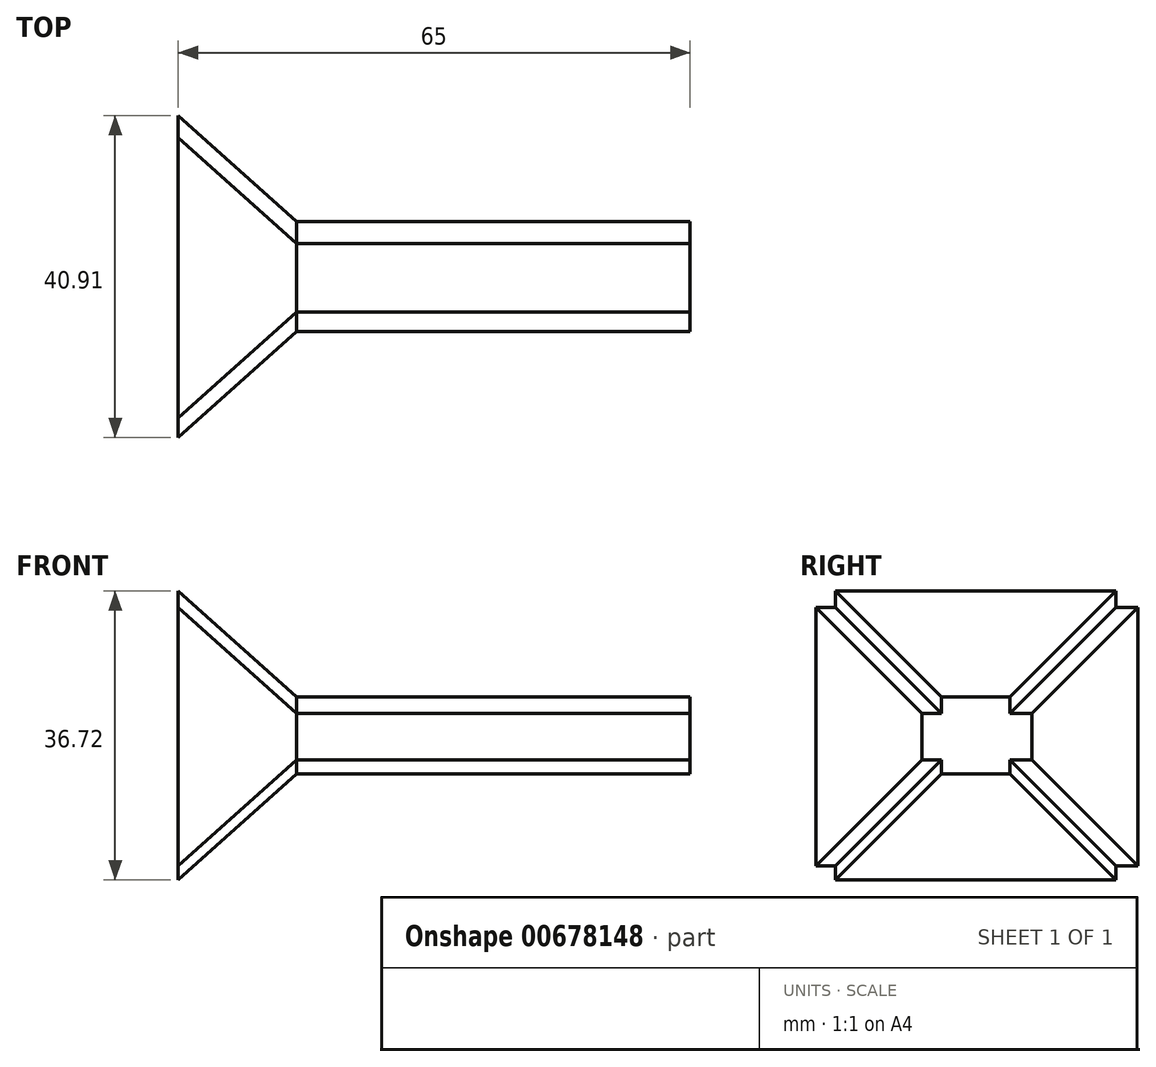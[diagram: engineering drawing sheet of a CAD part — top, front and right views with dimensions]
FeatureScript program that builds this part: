
annotation { "Feature Type Name" : "Feature", "Feature Type Description" : "" }
export const myFeature = defineFeature(function(context is Context, id is Id, definition is map)
    precondition{}
    {
        {
            var Q0;
            Q0=qCreatedBy(makeId("Right.planeOp"),FACE);
            var sketch = newSketch(context, id + "F0", { "sketchPlane" : qUnion([Q0])});
            skLineSegment(sketch, "E0.bottom", {"start": v(-4.45, 4.98) * mm, "end": v(4.28, 4.98) * mm});
            skLineSegment(sketch, "E0.top", {"start": v(-4.45, -4.82) * mm, "end": v(4.28, -4.82) * mm});
            skLineSegment(sketch, "E0.left", {"start": v(-4.45, 4.98) * mm, "end": v(-4.45, -4.82) * mm});
            skLineSegment(sketch, "E0.right", {"start": v(4.28, 4.98) * mm, "end": v(4.28, -4.82) * mm});
            skLineSegment(sketch, "E1.bottom", {"start": v(-6.9, 2.87) * mm, "end": v(7.08, 2.87) * mm});
            skLineSegment(sketch, "E1.top", {"start": v(-6.9, -3.03) * mm, "end": v(7.08, -3.03) * mm});
            skLineSegment(sketch, "E1.left", {"start": v(-6.9, 2.87) * mm, "end": v(-6.9, -3.03) * mm});
            skLineSegment(sketch, "E1.right", {"start": v(7.08, 2.87) * mm, "end": v(7.08, -3.03) * mm});
            skSolve(sketch);
        }
        {
            var Q0;
            {var subQ0=sQuery(id+"F0.wireOp",EDGE,"E0.bottom");Q0=makeQuery(id+"F0.imprint","IMPRINT",FACE,{"disambiguationData":[TD([[makeQuery(id+"F0.imprint","IMPRINT",EDGE,{"derivedFrom":subQ0}),-1.0]])]});}
            var Q1;
            {var subQ0=sQuery(id+"F0.wireOp",EDGE,"E0.top");Q1=makeQuery(id+"F0.imprint","IMPRINT",FACE,{"disambiguationData":[TD([[makeQuery(id+"F0.imprint","IMPRINT",EDGE,{"derivedFrom":subQ0}),1.0]])]});}
            var Q2;
            {var subQ5=sQuery(id+"F0.wireOp",EDGE,"E1.left");Q2=makeQuery(id+"F0.imprint","IMPRINT",FACE,{"disambiguationData":[TD([[makeQuery(id+"F0.imprint","IMPRINT",EDGE,{"derivedFrom":subQ5}),1.0]])]});}
            var Q3;
            {var subQ5=sQuery(id+"F0.wireOp",EDGE,"E1.right");Q3=makeQuery(id+"F0.imprint","IMPRINT",FACE,{"disambiguationData":[TD([[makeQuery(id+"F0.imprint","IMPRINT",EDGE,{"derivedFrom":subQ5}),-1.0]])]});}
            var Q4;
            {var subQ0=sQuery(id+"F0.wireOp",EDGE,"E1.bottom");var subQ1=sQuery(id+"F0.wireOp",EDGE,"E0.left");var subQ2=makeQuery(id+"F0.imprint","INTERSECT",VERTEX,{"derivedFrom":[subQ1,subQ0]});Q4=makeQuery(id+"F0.imprint","IMPRINT",FACE,{"disambiguationData":[TD([[makeQuery(id+"F0.imprint","IMPRINT",EDGE,{"disambiguationData":[TD([[subQ2,-1.0]])],"derivedFrom":subQ1}),1.0]])]});}
            extrude(context, id + "F1", {"entities" : qUnion([Q0, Q1, Q2, Q3, Q4]), "depth" : 50 * mm, "offsetDistance" : 25 * mm});
        }
        {
            var Q0;
            Q0=makeQuery(id+"F1.opExtrude","CAP_FACE",FACE,{"disambiguationData":[OSD([sQuery(id+"F0.wireOp",EDGE,"E0.bottom"),sQuery(id+"F0.wireOp",EDGE,"E0.top"),sQuery(id+"F0.wireOp",EDGE,"E0.left"),sQuery(id+"F0.wireOp",EDGE,"E0.right"),sQuery(id+"F0.wireOp",EDGE,"E1.bottom"),sQuery(id+"F0.wireOp",EDGE,"E1.top"),sQuery(id+"F0.wireOp",EDGE,"E1.left"),sQuery(id+"F0.wireOp",EDGE,"E1.right")])],"isStart":true});
            extrude(context, id + "F2", {"entities" : qUnion([Q0]), "operationType" : NewBodyOperationType.ADD, "depth" : 15 * mm, "offsetDistance" : 25 * mm, "hasDraft" : true, "draftAngle" : 41.9 * degree});
        }
    });
